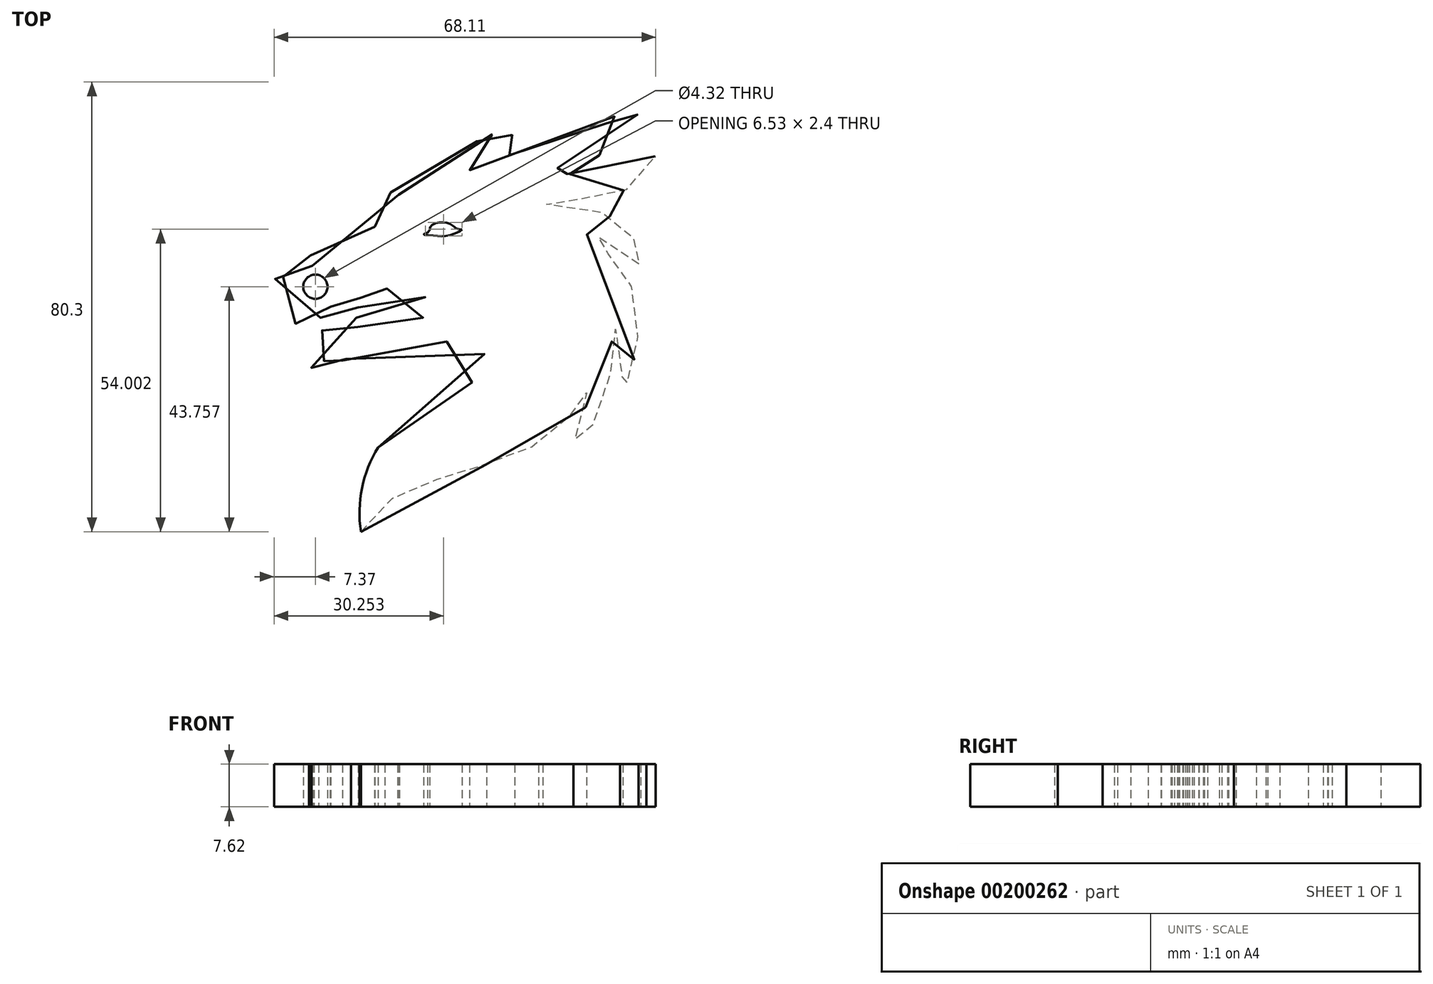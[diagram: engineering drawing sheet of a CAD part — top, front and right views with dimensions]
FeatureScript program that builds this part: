
annotation { "Feature Type Name" : "Feature", "Feature Type Description" : "" }
export const myFeature = defineFeature(function(context is Context, id is Id, definition is map)
    precondition{}
    {
        {
            var Q0;
            Q0=qCreatedBy(makeId("Top.planeOp"),FACE);
            var sketch = newSketch(context, id + "F0", { "sketchPlane" : qUnion([Q0])});
            skArc(sketch, "E0", {"start": v(-34.09, -25.74) * mm, "mid": v(-36.96, -32.98) * mm, "end": v(-37.16, -40.78) * mm});
            skFitSpline(sketch, "E1", {"points": [v(-37.16, -40.78) * mm, v(-33.88, -36.97) * mm, v(-30.17, -33.9) * mm, v(-24.66, -31.77) * mm, v(-20.1, -30.19) * mm, v(-15.76, -29.02) * mm, v(-8.87, -26.78) * mm, v(-2.63, -22.86) * mm, v(0.64, -19.2) * mm, v(2.9, -14.5) * mm, v(2.93, -18.46) * mm, v(1.44, -23.36) * mm, v(0.82, -25.18) * mm, v(2.81, -23.57) * mm, v(5.1, -20.12) * mm, v(7.36, -12.88) * mm, v(7.86, -3.83) * mm, v(9.1, -7.58) * mm, v(9.5, -12.63) * mm, v(9.16, -17.18) * mm, v(10.46, -13.88) * mm, v(11.76, -9.38) * mm, v(12.4, -3.13) * mm, v(11.26, 2.77) * mm, v(9.16, 6.57) * mm, v(6.5, 9.27) * mm, v(3.1, 12.22) * mm, v(6.46, 11.42) * mm, v(10.76, 8.72) * mm, v(13.7, 6.27) * mm, v(12.2, 10.52) * mm, v(9.86, 13.47) * mm, v(6.1, 16.12) * mm, v(0.56, 16.92) * mm, v(-5.44, 18.17) * mm, v(0.9, 18.52) * mm, v(7.46, 19.52) * mm, v(12.6, 21.97) * mm, v(15.46, 26.32) * mm, v(14.3, 25.22) * mm, v(10.36, 23.77) * mm, v(4.8, 23.02) * mm, v(0.46, 23.07) * mm, v(-4.24, 22.92) * mm, v(-9.7, 22.27) * mm, v(-5.64, 23.77) * mm, v(-1.24, 24.22) * mm, v(3.76, 25.67) * mm, v(8.6, 28.82) * mm, v(11.76, 32.87) * mm, v(12.76, 36.27) * mm, v(12.3, 39.52) * mm, v(11.46, 37.97) * mm, v(8.86, 34.12) * mm, v(4.16, 30.42) * mm, v(-0.94, 28.32) * mm, v(-6.3, 27.52) * mm, v(-12, 25.97) * mm, v(-17.74, 23.82) * mm, v(-14.44, 27.07) * mm, v(-11.54, 29.37) * mm, v(-7.54, 31.12) * mm, v(-4.7, 32.47) * mm, v(-10.7, 31.27) * mm, v(-16.94, 28.67) * mm, v(-21.2, 26.07) * mm, v(-25.59, 22.22) * mm, v(-29.99, 20.22) * mm, v(-32.84, 19.52) * mm, v(-30.39, 19.37) * mm, v(-30.54, 18.32) * mm, v(-30.54, 17.12) * mm, v(-32.09, 14.92) * mm, v(-35.09, 13.57) * mm, v(-39.49, 11.62) * mm, v(-43.29, 9.17) * mm, v(-46.19, 6.67) * mm, v(-46.14, 8.57) * mm, v(-44.69, 10.27) * mm, v(-47.29, 9.12) * mm, v(-48.79, 6.57) * mm, v(-50.39, 3.67) * mm, v(-50.94, 4.67) * mm, v(-52.59, 5.22) * mm, v(-51.79, 3.12) * mm, v(-50.89, 0.42) * mm, v(-49.29, -4.78) * mm, v(-48.84, -3.68) * mm, v(-47.24, -1.93) * mm, v(-45.64, -1.28) * mm, v(-45.64, -3.63) * mm, v(-44.59, -2.88) * mm, v(-42.59, 0) * mm, v(-42.54, -2.78) * mm, v(-41.09, -1.73) * mm, v(-40.14, 0) * mm, v(-39.84, -1.93) * mm, v(-38.74, -1.13) * mm, v(-37.16, 0.97) * mm, v(-37.64, -0.78) * mm, v(-36.39, 0) * mm, v(-35.39, 1.57) * mm, v(-35.19, 0) * mm, v(-33.99, 1.22) * mm, v(-31.59, 3.22) * mm, v(-29.29, 4.12) * mm, v(-27.39, 3.02) * mm, v(-25.49, 0.62) * mm, v(-25.59, -2.68) * mm, v(-26.39, -2.38) * mm, v(-30.09, -2.28) * mm, v(-34.64, -3.48) * mm, v(-34.74, -1.68) * mm, v(-37.59, -4.33) * mm, v(-38.09, -2.38) * mm, v(-40.49, -4.98) * mm, v(-41.04, -3.48) * mm, v(-43.74, -6.73) * mm, v(-44.04, -4.88) * mm, v(-46.29, -8.18) * mm, v(-45.99, -12.18) * mm, v(-45.99, -10.58) * mm, v(-45.04, -9.03) * mm, v(-43.64, -10.38) * mm, v(-41.54, -11.38) * mm, v(-40.34, -13.08) * mm, v(-39.59, -15.08) * mm, v(-38.99, -12.53) * mm, v(-40.44, -10.28) * mm, v(-35.09, -9.33) * mm, v(-29.44, -7.98) * mm, v(-23.4, -7.03) * mm, v(-19.54, -6.73) * mm, v(-16, -7.83) * mm, v(-14.94, -9.53) * mm, v(-14.9, -11.78) * mm, v(-17.5, -14.23) * mm, v(-23.94, -18.28) * mm, v(-29.84, -21.53) * mm, v(-34.09, -25.74) * mm], "startDerivative": vector(384.35, 464.21) * mm, "endDerivative": vector(-429.19, -495.54) * mm});
            skSolve(sketch);
        }
        {
            var Q0;
            Q0=makeQuery(id+"F0.imprint","IMPRINT",FACE,{"disambiguationData":[TD([[makeQuery(id+"F0.imprint","IMPRINT",EDGE,{"derivedFrom":sQuery(id+"F0.wireOp",EDGE,"E0")}),1.0]])]});
            extrude(context, id + "F1", {"entities" : qUnion([Q0]), "depth" : 7.62 * mm});
        }
        {
            var Q0;
            Q0=qCreatedBy(makeId("Top.planeOp"),FACE);
            var sketch = newSketch(context, id + "F2", { "sketchPlane" : qUnion([Q0])});
            skFitSpline(sketch, "E2", {"points": [v(-19.13, 13.16) * mm, v(-20.78, 12.34) * mm, v(-22.75, 12) * mm, v(-24.62, 12.12) * mm, v(-26, 12.32) * mm, v(-24.96, 12.9) * mm, v(-24.83, 13.59) * mm, v(-23.78, 14.34) * mm, v(-22.36, 14.43) * mm, v(-21.15, 14.15) * mm, v(-19.88, 13.28) * mm, v(-19.13, 13.16) * mm]});
            skCircle(sketch, "E3", {"center": v(-45.28, 2.98) * mm, "radius": 2.16 * mm});
            skSolve(sketch);
        }
        {
            var Q0;
            Q0=makeQuery(id+"F2.imprint","IMPRINT",FACE,{"disambiguationData":[TD([[makeQuery(id+"F2.imprint","IMPRINT",EDGE,{"derivedFrom":sQuery(id+"F2.wireOp",EDGE,"E2")}),-1.0]])]});
            var Q1;
            Q1=makeQuery(id+"F2.imprint","IMPRINT",FACE,{"disambiguationData":[TD([[makeQuery(id+"F2.imprint","IMPRINT",EDGE,{"derivedFrom":sQuery(id+"F2.wireOp",EDGE,"E3")}),1.0]])]});
            extrude(context, id + "F3", {"entities" : qUnion([Q0, Q1]), "operationType" : NewBodyOperationType.REMOVE, "depth" : 7.98 * mm});
        }
    });
